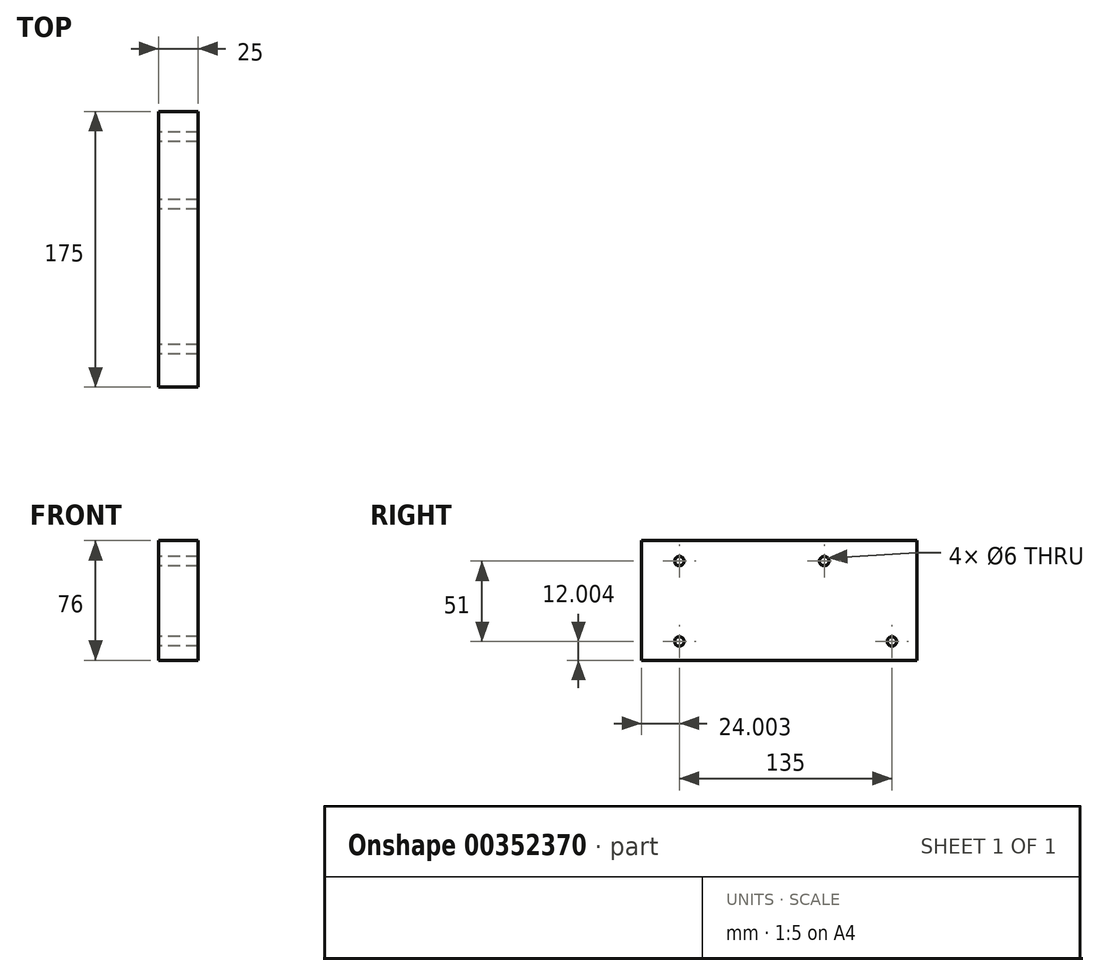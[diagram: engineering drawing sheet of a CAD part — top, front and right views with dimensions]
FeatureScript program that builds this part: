
annotation { "Feature Type Name" : "Feature", "Feature Type Description" : "" }
export const myFeature = defineFeature(function(context is Context, id is Id, definition is map)
    precondition{}
    {
        {
            var Q0;
            Q0=qCreatedBy(makeId("Right.planeOp"),FACE);
            var sketch = newSketch(context, id + "F0", { "sketchPlane" : qUnion([Q0])});
            skLineSegment(sketch, "E0.bottom", {"start": v(-92.08, 41.65) * mm, "end": v(82.92, 41.65) * mm});
            skLineSegment(sketch, "E0.top", {"start": v(-92.08, -34.35) * mm, "end": v(82.92, -34.35) * mm});
            skLineSegment(sketch, "E0.left", {"start": v(-92.08, 41.65) * mm, "end": v(-92.08, -34.35) * mm});
            skLineSegment(sketch, "E0.right", {"start": v(82.92, 41.65) * mm, "end": v(82.92, -34.35) * mm});
            skCircle(sketch, "E1", {"center": v(-68.08, 28.65) * mm, "radius": 3 * mm});
            skCircle(sketch, "E2", {"center": v(-68.08, -22.35) * mm, "radius": 3 * mm});
            skCircle(sketch, "E3", {"center": v(23.92, 28.65) * mm, "radius": 3 * mm});
            skCircle(sketch, "E4", {"center": v(66.92, -22.35) * mm, "radius": 3 * mm});
            skSolve(sketch);
        }
        {
            var Q0;
            Q0=makeQuery(id+"F0.imprint","IMPRINT",FACE,{"disambiguationData":[TD([[makeQuery(id+"F0.imprint","IMPRINT",EDGE,{"derivedFrom":sQuery(id+"F0.wireOp",EDGE,"E0.bottom")}),-1.0]])]});
            extrude(context, id + "F1", {"entities" : qUnion([Q0]), "depth" : 25 * mm});
        }
    });
